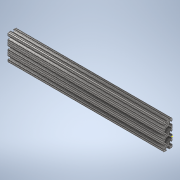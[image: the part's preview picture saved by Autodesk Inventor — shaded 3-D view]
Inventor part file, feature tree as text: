
AUTODESK INVENTOR PART (.ipt)
format: ipt  version: 2020 (Build 240168000, 168)  size: 380,928 bytes
history: native  units: in
note: dims shown in document units (in); Inventor stores cm internally (conversion verified against a paired STEP export)
features: sketch x2, extrude x1
ambient origin geometry x8: Origin, YZ Plane, XZ Plane, XY Plane, X Axis, Y Axis, Z Axis, Center Point
bodies: Solid1 (feature_tree)
feature tree (3):
  extrude  "Extrusion1"  [1 undecoded]
  sketch  "Sketch2"
  sketch  "Sketch1"  dims[d0=18.0in d1=0.0in]
note: 1 required parameter value undecoded (feature->parameter linkage not recoverable at this tier; creation-order binding heuristic only, values carry confidence <= 0.55)
